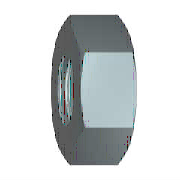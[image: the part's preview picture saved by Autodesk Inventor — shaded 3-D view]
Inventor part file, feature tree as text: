
AUTODESK INVENTOR PART (.ipt)
format: ipt  version: 2023 (Build 270158000, 158)  size: 172,544 bytes
history: native  units: mm (DEFAULTED — no unit token found)
features: sketch x3, other x2, extrude x1, hole x1, plane x1
ambient origin geometry x7: Origin, YZ Plane, XZ Plane, X Axis, Y Axis, Z Axis, Center Point
bodies: Solid1 (feature_tree)
feature tree (8):
  extrude  "Базовый элемент"  Depth=20.78461mm
  other  "Фаска1"
  hole  "Резьба"  [1 undecoded]
  other  "Work Axis1"
  plane  "Work Plane1"
  sketch  "Эскиз1"
  sketch  "Эскиз2"
  sketch  "Эскиз3"
note: 1 required parameter value undecoded (feature->parameter linkage not recoverable at this tier; creation-order binding heuristic only, values carry confidence <= 0.55)
